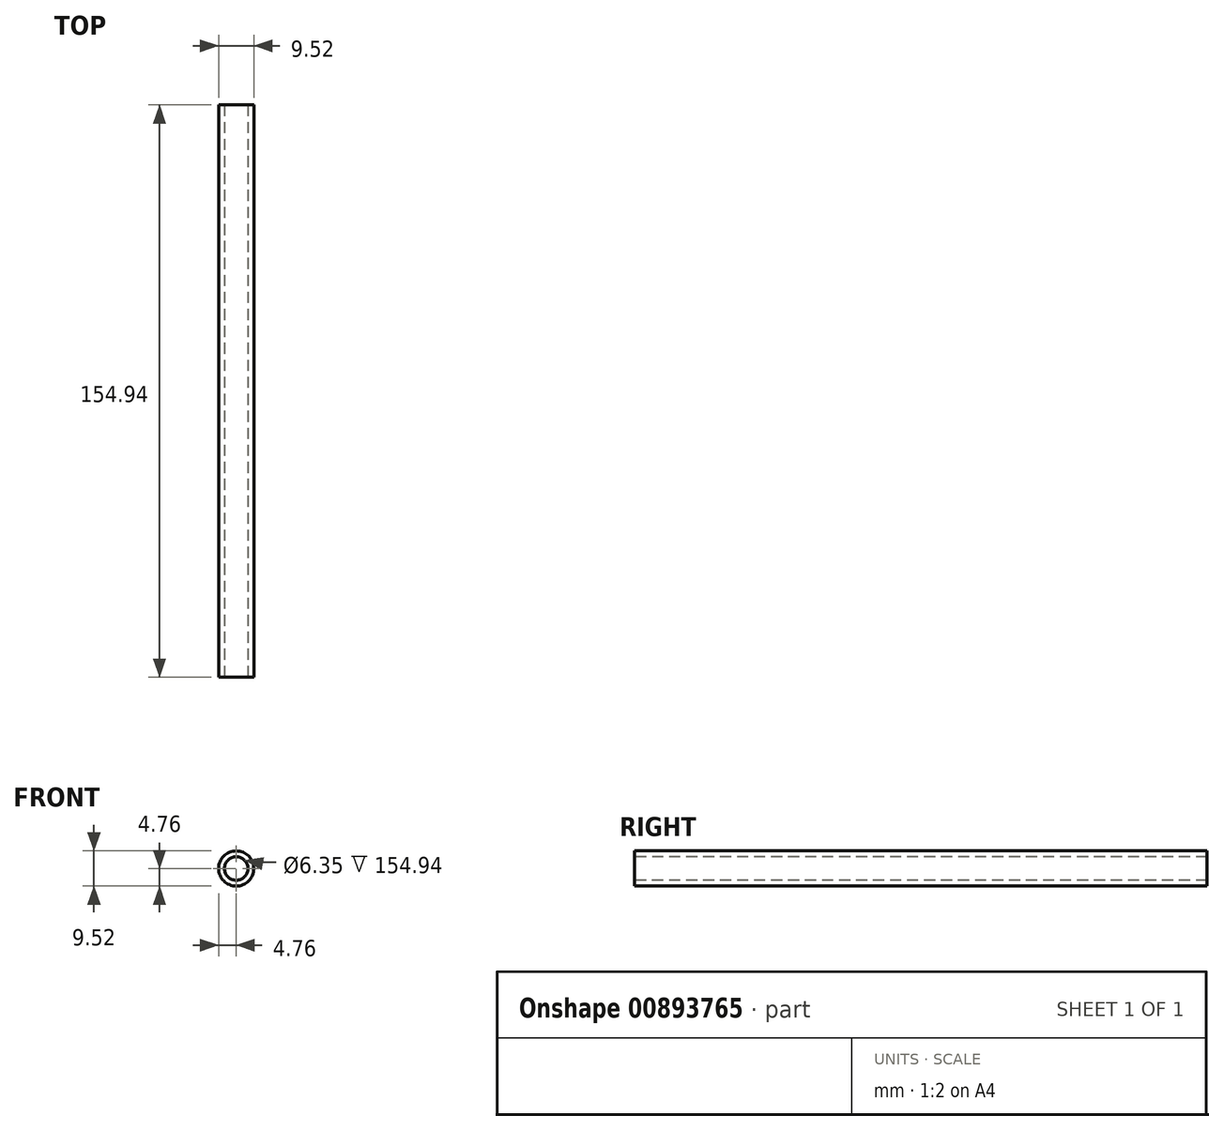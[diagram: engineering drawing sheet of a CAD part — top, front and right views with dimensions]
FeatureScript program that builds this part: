
annotation { "Feature Type Name" : "Feature", "Feature Type Description" : "" }
export const myFeature = defineFeature(function(context is Context, id is Id, definition is map)
    precondition{}
    {
        {
            var Q0;
            Q0=qCreatedBy(makeId("Front.planeOp"),FACE);
            var sketch = newSketch(context, id + "F0", { "sketchPlane" : qUnion([Q0])});
            skCircle(sketch, "E0", {"center": v(0, 0) * mm, "radius": 4.76 * mm});
            skSolve(sketch);
        }
        {
            var Q0;
            Q0 = qSketchRegion(id + "F0", true);
            extrude(context, id + "F1", {"entities" : qUnion([Q0]), "depth" : 78.74 * mm, "offsetDistance" : 25.4 * mm, "hasSecondDirection" : true, "secondDirectionOppositeDirection" : true, "secondDirectionDepth" : 76.2 * mm});
        }
        {
            var Q0;
            Q0=makeQuery(id+"F1.opExtrude","CAP_FACE",FACE,{"disambiguationData":[OSD([sQuery(id+"F0.wireOp",EDGE,"E0")])],"isStart":false});
            var sketch = newSketch(context, id + "F2", { "sketchPlane" : qUnion([Q0])});
            skCircle(sketch, "E1", {"center": v(0, 0) * mm, "radius": 3.18 * mm});
            skSolve(sketch);
        }
        {
            var Q0;
            Q0 = qSketchRegion(id + "F2", true);
            extrude(context, id + "F3", {"entities" : qUnion([Q0]), "operationType" : NewBodyOperationType.REMOVE, "oppositeDirection" : true, "depth" : 255.02 * mm, "offsetDistance" : 25.4 * mm});
        }
    });
